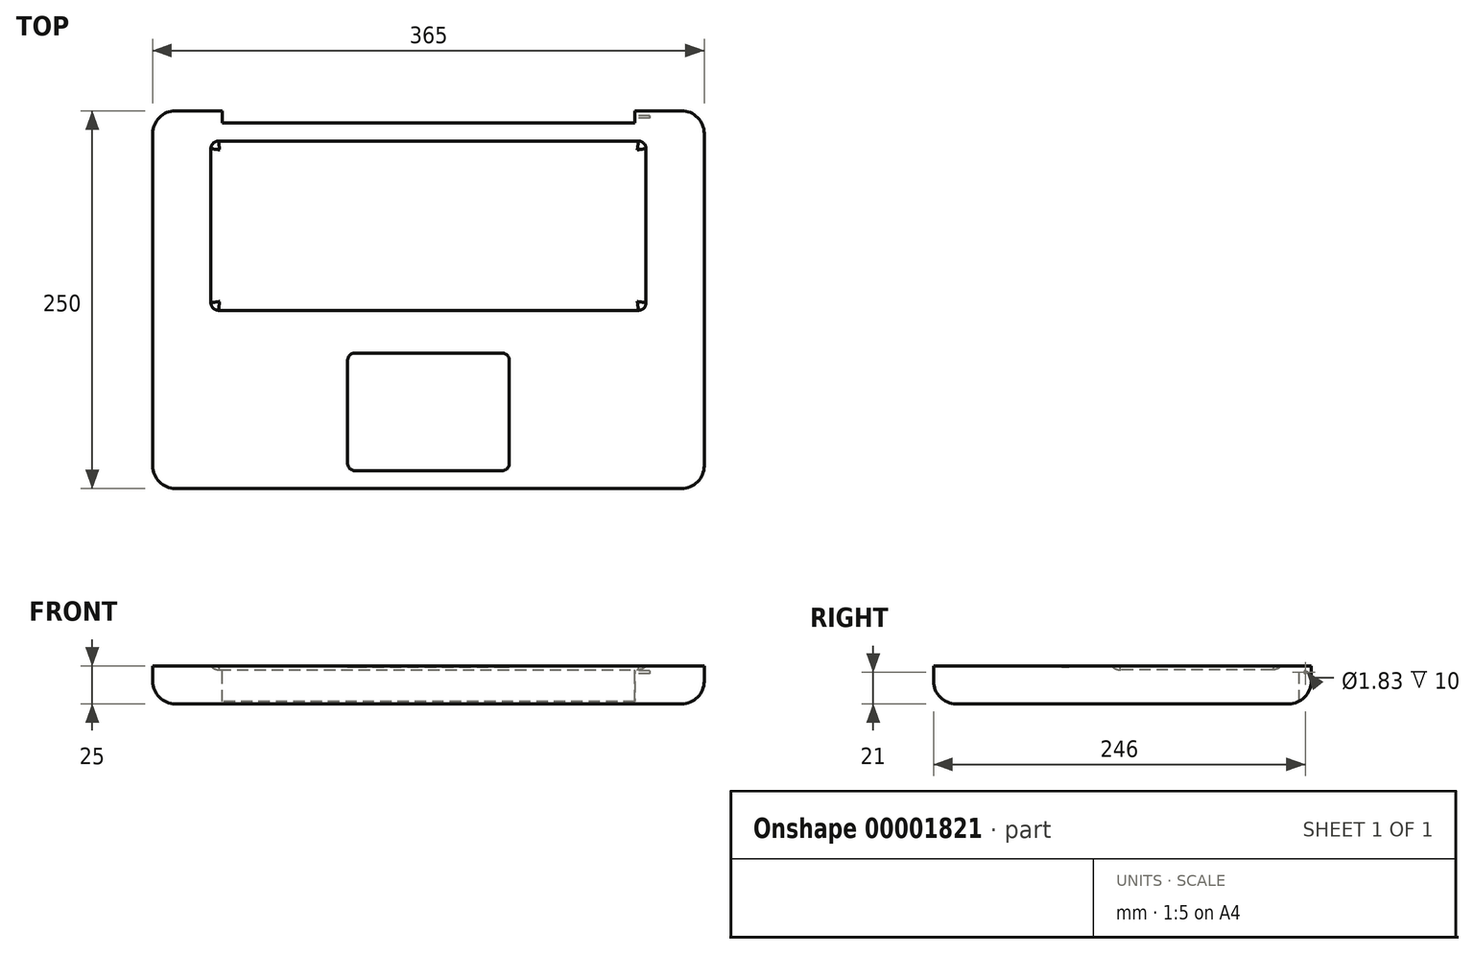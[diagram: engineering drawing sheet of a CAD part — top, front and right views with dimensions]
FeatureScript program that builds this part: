
annotation { "Feature Type Name" : "Feature", "Feature Type Description" : "" }
export const myFeature = defineFeature(function(context is Context, id is Id, definition is map)
    precondition{}
    {
        {
            var Q0;
            Q0=qCreatedBy(makeId("Top.planeOp"),FACE);
            var sketch = newSketch(context, id + "F0", { "sketchPlane" : qUnion([Q0])});
            skLineSegment(sketch, "E0.rect.bottom", {"start": v(167.5, -125) * mm, "end": v(-167.5, -125) * mm});
            skLineSegment(sketch, "E0.rect.top", {"start": v(167.5, 125) * mm, "end": v(-167.5, 125) * mm});
            skLineSegment(sketch, "E0.rect.left", {"start": v(182.5, -110) * mm, "end": v(182.5, 110) * mm});
            skLineSegment(sketch, "E0.rect.right", {"start": v(-182.5, -110) * mm, "end": v(-182.5, 110) * mm});
            skPoint(sketch, "E0.rect.middle", {"position": v(0, 0) * mm});
            skPoint(sketch, "E1.visualSharp", {"position": v(-182.5, 125) * mm});
            skArc(sketch, "E1.filletArc", {"start": v(-167.5, 125) * mm, "mid": v(-178.1, 120.6) * mm, "end": v(-182.5, 110) * mm});
            skPoint(sketch, "E2.visualSharp", {"position": v(-182.5, -125) * mm});
            skArc(sketch, "E2.filletArc", {"start": v(-182.5, -110) * mm, "mid": v(-178.1, -120.6) * mm, "end": v(-167.5, -125) * mm});
            skPoint(sketch, "E3.visualSharp", {"position": v(182.5, 125) * mm});
            skArc(sketch, "E3.filletArc", {"start": v(182.5, 110) * mm, "mid": v(178.1, 120.6) * mm, "end": v(167.5, 125) * mm});
            skPoint(sketch, "E4.visualSharp", {"position": v(182.5, -125) * mm});
            skArc(sketch, "E4.filletArc", {"start": v(167.5, -125) * mm, "mid": v(178.1, -120.6) * mm, "end": v(182.5, -110) * mm});
            skSolve(sketch);
        }
        {
            var Q0;
            Q0 = qSketchRegion(id + "F0", true);
            extrude(context, id + "F1", {"entities" : qUnion([Q0]), "depth" : 25 * mm});
        }
        {
            var Q0;
            Q0=makeQuery(id+"F1.opExtrude","CAP_EDGE",EDGE,{"disambiguationData":[OSD([sQuery(id+"F0.wireOp",EDGE,"E0.rect.bottom")])],"isStart":true});
            fillet(context, id + "F2", {"entities" : qUnion([Q0]), "radius" : 15 * mm, "tangentPropagation" : true, "allowEdgeOverflow" : false});
        }
        {
            var Q0;
            Q0=makeQuery(id+"F1.opExtrude","CAP_FACE",FACE,{"disambiguationData":[OSD([sQuery(id+"F0.wireOp",EDGE,"E0.rect.bottom"),sQuery(id+"F0.wireOp",EDGE,"E0.rect.top"),sQuery(id+"F0.wireOp",EDGE,"E0.rect.left"),sQuery(id+"F0.wireOp",EDGE,"E0.rect.right"),sQuery(id+"F0.wireOp",EDGE,"E1.filletArc"),sQuery(id+"F0.wireOp",EDGE,"E2.filletArc"),sQuery(id+"F0.wireOp",EDGE,"E3.filletArc"),sQuery(id+"F0.wireOp",EDGE,"E4.filletArc")])],"isStart":false});
            var sketch = newSketch(context, id + "F3", { "sketchPlane" : qUnion([Q0])});
            skLineSegment(sketch, "E5", {"start": v(-136.5, 117) * mm, "end": v(-136.5, 125) * mm});
            skLineSegment(sketch, "E6", {"start": v(-136.5, 125) * mm, "end": v(136.5, 125) * mm});
            skLineSegment(sketch, "E7", {"start": v(136.5, 125) * mm, "end": v(136.5, 117) * mm});
            skLineSegment(sketch, "E8", {"start": v(-136.5, 117) * mm, "end": v(136.5, 117) * mm});
            skLineSegment(sketch, "E9", {"start": v(-136.5, 125) * mm, "end": v(-182.5, 125) * mm, "construction": true});
            skLineSegment(sketch, "E10", {"start": v(136.5, 125) * mm, "end": v(182.5, 125) * mm, "construction": true});
            skSolve(sketch);
        }
        {
            var Q0;
            Q0 = qSketchRegion(id + "F3", true);
            extrude(context, id + "F4", {"entities" : qUnion([Q0]), "operationType" : NewBodyOperationType.REMOVE, "endBound" : BoundingType.THROUGH_ALL, "oppositeDirection" : true, "depth" : 25 * mm});
        }
        {
            var Q0;
            Q0=makeQuery(id+"F1.opExtrude","CAP_FACE",FACE,{"disambiguationData":[OSD([sQuery(id+"F0.wireOp",EDGE,"E0.rect.bottom"),sQuery(id+"F0.wireOp",EDGE,"E0.rect.top"),sQuery(id+"F0.wireOp",EDGE,"E0.rect.left"),sQuery(id+"F0.wireOp",EDGE,"E0.rect.right"),sQuery(id+"F0.wireOp",EDGE,"E1.filletArc"),sQuery(id+"F0.wireOp",EDGE,"E2.filletArc"),sQuery(id+"F0.wireOp",EDGE,"E3.filletArc"),sQuery(id+"F0.wireOp",EDGE,"E4.filletArc")])],"isStart":false});
            var sketch = newSketch(context, id + "F5", { "sketchPlane" : qUnion([Q0])});
            skLineSegment(sketch, "E11.bottom", {"start": v(-139, 105) * mm, "end": v(139, 105) * mm});
            skLineSegment(sketch, "E11.top", {"start": v(-139, -7) * mm, "end": v(139, -7) * mm});
            skLineSegment(sketch, "E11.left", {"start": v(-144, 100) * mm, "end": v(-144, -2) * mm});
            skLineSegment(sketch, "E11.right", {"start": v(144, 100) * mm, "end": v(144, -2) * mm});
            skLineSegment(sketch, "E12", {"start": v(0, 105) * mm, "end": v(0, 117) * mm, "construction": true});
            skPoint(sketch, "E13.visualSharp", {"position": v(-144, -7) * mm});
            skArc(sketch, "E13.filletArc", {"start": v(-144, -2) * mm, "mid": v(-142.54, -5.54) * mm, "end": v(-139, -7) * mm});
            skPoint(sketch, "E14.visualSharp", {"position": v(-144, 105) * mm});
            skArc(sketch, "E14.filletArc", {"start": v(-139, 105) * mm, "mid": v(-142.54, 103.54) * mm, "end": v(-144, 100) * mm});
            skPoint(sketch, "E15.visualSharp", {"position": v(144, 105) * mm});
            skArc(sketch, "E15.filletArc", {"start": v(144, 100) * mm, "mid": v(142.54, 103.54) * mm, "end": v(139, 105) * mm});
            skPoint(sketch, "E16.visualSharp", {"position": v(144, -7) * mm});
            skArc(sketch, "E16.filletArc", {"start": v(139, -7) * mm, "mid": v(142.54, -5.54) * mm, "end": v(144, -2) * mm});
            skSolve(sketch);
        }
        {
            var Q0;
            Q0 = qSketchRegion(id + "F5", true);
            extrude(context, id + "F6", {"entities" : qUnion([Q0]), "operationType" : NewBodyOperationType.REMOVE, "oppositeDirection" : true, "depth" : 2.5 * mm});
        }
        {
            var Q0;
            Q0=makeQuery(id+"F6.boolean.opBoolean","COPY",EDGE,{"derivedFrom":makeQuery(id+"F6.opExtrude","CAP_EDGE",EDGE,{"disambiguationData":[OSD([sQuery(id+"F5.wireOp",EDGE,"E11.bottom")])],"isStart":false})});
            fillet(context, id + "F7", {"entities" : qUnion([Q0]), "radius" : 8 * mm, "tangentPropagation" : true, "allowEdgeOverflow" : false});
        }
        {
            var Q0;
            Q0=makeQuery(id+"F1.opExtrude","CAP_FACE",FACE,{"disambiguationData":[OSD([sQuery(id+"F0.wireOp",EDGE,"E0.rect.bottom"),sQuery(id+"F0.wireOp",EDGE,"E0.rect.top"),sQuery(id+"F0.wireOp",EDGE,"E0.rect.left"),sQuery(id+"F0.wireOp",EDGE,"E0.rect.right"),sQuery(id+"F0.wireOp",EDGE,"E1.filletArc"),sQuery(id+"F0.wireOp",EDGE,"E2.filletArc"),sQuery(id+"F0.wireOp",EDGE,"E3.filletArc"),sQuery(id+"F0.wireOp",EDGE,"E4.filletArc")])],"isStart":false});
            var sketch = newSketch(context, id + "F8", { "sketchPlane" : qUnion([Q0])});
            skLineSegment(sketch, "E17.bottom", {"start": v(-48.5, -35.24) * mm, "end": v(48.5, -35.24) * mm});
            skLineSegment(sketch, "E17.top", {"start": v(-48.5, -113.24) * mm, "end": v(48.5, -113.24) * mm});
            skLineSegment(sketch, "E17.left", {"start": v(-53.5, -40.24) * mm, "end": v(-53.5, -108.24) * mm});
            skLineSegment(sketch, "E17.right", {"start": v(53.5, -40.24) * mm, "end": v(53.5, -108.24) * mm});
            skLineSegment(sketch, "E18", {"start": v(0, -113.24) * mm, "end": v(0, -125) * mm, "construction": true});
            skPoint(sketch, "E19.visualSharp", {"position": v(-53.5, -35.24) * mm});
            skArc(sketch, "E19.filletArc", {"start": v(-48.5, -35.24) * mm, "mid": v(-52.04, -36.7) * mm, "end": v(-53.5, -40.24) * mm});
            skPoint(sketch, "E20.visualSharp", {"position": v(-53.5, -113.24) * mm});
            skArc(sketch, "E20.filletArc", {"start": v(-53.5, -108.24) * mm, "mid": v(-52.04, -111.78) * mm, "end": v(-48.5, -113.24) * mm});
            skPoint(sketch, "E21.visualSharp", {"position": v(53.5, -113.24) * mm});
            skArc(sketch, "E21.filletArc", {"start": v(48.5, -113.24) * mm, "mid": v(52.04, -111.78) * mm, "end": v(53.5, -108.24) * mm});
            skPoint(sketch, "E22.visualSharp", {"position": v(53.5, -35.24) * mm});
            skArc(sketch, "E22.filletArc", {"start": v(53.5, -40.24) * mm, "mid": v(52.04, -36.7) * mm, "end": v(48.5, -35.24) * mm});
            skSolve(sketch);
        }
        {
            var Q0;
            Q0 = qSketchRegion(id + "F8", true);
            extrude(context, id + "F9", {"entities" : qUnion([Q0]), "operationType" : NewBodyOperationType.REMOVE, "oppositeDirection" : true, "depth" : 0.5 * mm});
        }
        {
            var Q0;
            Q0=makeQuery(id+"F4.boolean.opBoolean","COPY",FACE,{"derivedFrom":makeQuery(id+"F4.opExtrude","SWEPT_FACE",FACE,{"disambiguationData":[OSD([sQuery(id+"F3.wireOp",EDGE,"E7")])]})});
            var sketch = newSketch(context, id + "F10", { "sketchPlane" : qUnion([Q0])});
            skLineSegment(sketch, "E23.bottom", {"start": v(-125, 25) * mm, "end": v(-117, 25) * mm});
            skLineSegment(sketch, "E23.top", {"start": v(-125, 17) * mm, "end": v(-117, 17) * mm});
            skLineSegment(sketch, "E23.left", {"start": v(-125, 25) * mm, "end": v(-125, 17) * mm});
            skLineSegment(sketch, "E23.right", {"start": v(-117, 25) * mm, "end": v(-117, 17) * mm});
            skLineSegment(sketch, "E24", {"start": v(-121, 25) * mm, "end": v(-121, 17) * mm, "construction": true});
            skLineSegment(sketch, "E25", {"start": v(-125, 21) * mm, "end": v(-117, 21) * mm, "construction": true});
            skCircle(sketch, "E26", {"center": v(-121, 21) * mm, "radius": 4 * mm, "construction": true});
            skCircle(sketch, "E27", {"center": v(-121, 21) * mm, "radius": 0.92 * mm});
            skSolve(sketch);
        }
        {
            var Q0;
            Q0=makeQuery(id+"F10.imprint","IMPRINT",FACE,{"disambiguationData":[TD([[makeQuery(id+"F10.imprint","IMPRINT",EDGE,{"derivedFrom":sQuery(id+"F10.wireOp",EDGE,"E27")}),1.0]])]});
            extrude(context, id + "F11", {"entities" : qUnion([Q0]), "operationType" : NewBodyOperationType.REMOVE, "oppositeDirection" : true, "depth" : 10 * mm});
        }
    });
